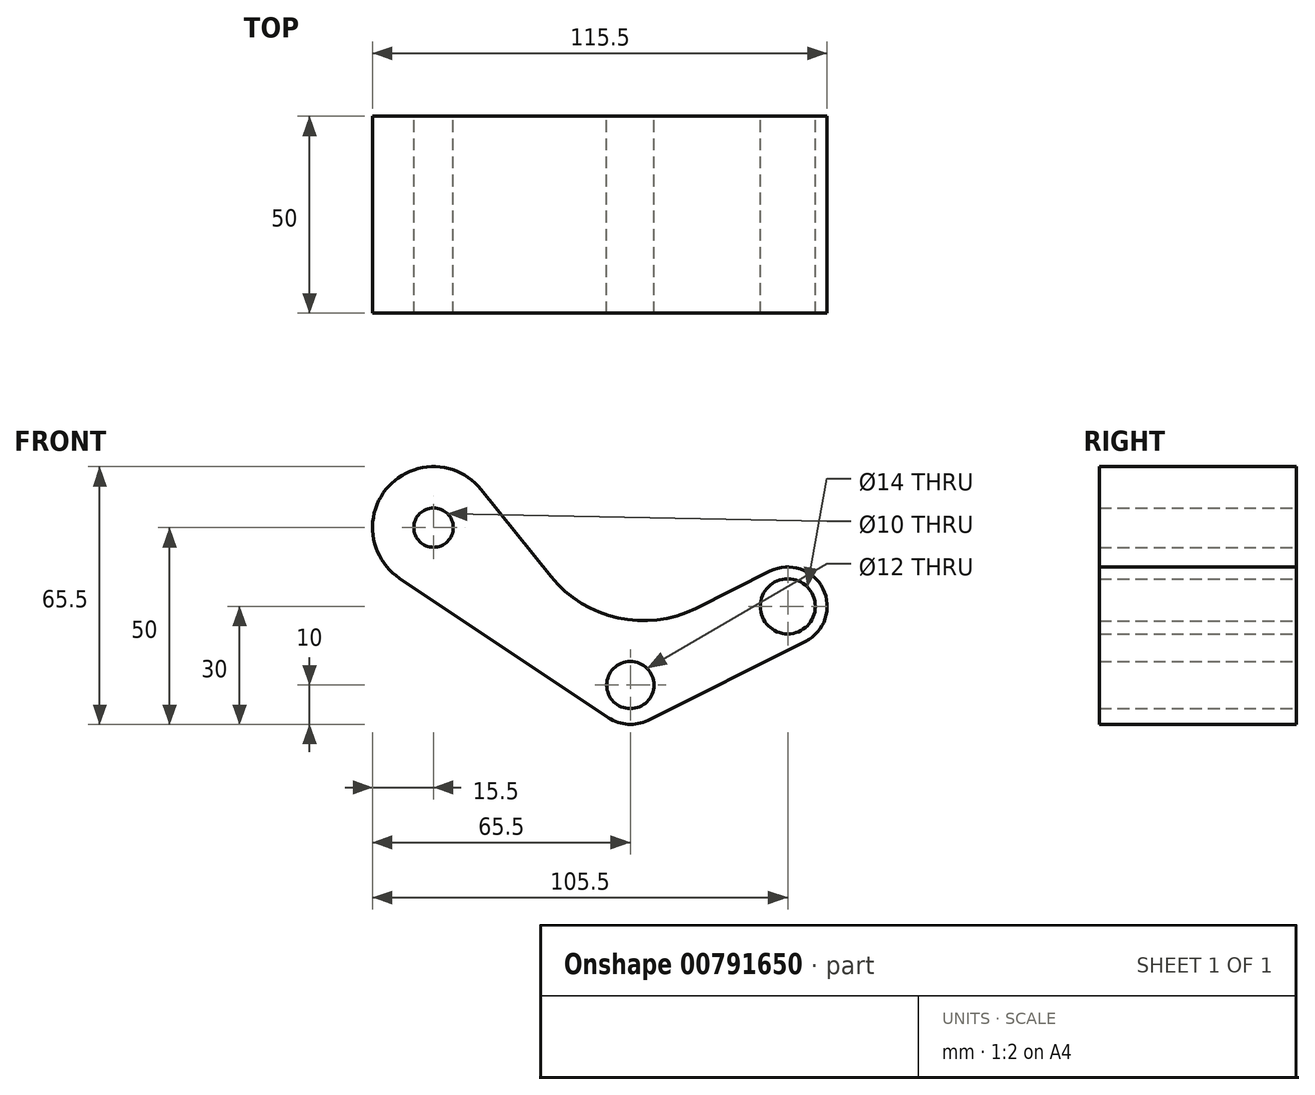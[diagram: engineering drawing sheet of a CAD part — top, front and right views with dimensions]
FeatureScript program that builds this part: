
annotation { "Feature Type Name" : "Feature", "Feature Type Description" : "" }
export const myFeature = defineFeature(function(context is Context, id is Id, definition is map)
    precondition{}
    {
        {
            var Q0;
            Q0=qCreatedBy(makeId("Front.planeOp"),FACE);
            var sketch = newSketch(context, id + "F0", { "sketchPlane" : qUnion([Q0])});
            skCircle(sketch, "E0", {"center": v(0, 0) * mm, "radius": 10 * mm});
            skCircle(sketch, "E1", {"center": v(0, 0) * mm, "radius": 6 * mm});
            skCircle(sketch, "E2", {"center": v(40, 20) * mm, "radius": 7 * mm});
            skCircle(sketch, "E3", {"center": v(40, 20) * mm, "radius": 10 * mm});
            skCircle(sketch, "E4", {"center": v(-50, 40) * mm, "radius": 15.5 * mm});
            skCircle(sketch, "E5", {"center": v(-50, 40) * mm, "radius": 5 * mm});
            skLineSegment(sketch, "E6", {"start": v(-58.6, 27.1) * mm, "end": v(-5.55, -8.32) * mm});
            skLineSegment(sketch, "E7", {"start": v(4.47, -8.94) * mm, "end": v(44.47, 11.06) * mm});
            skLineSegment(sketch, "E8", {"start": v(-37.91, 49.7) * mm, "end": v(-20.15, 27.57) * mm});
            skLineSegment(sketch, "E9", {"start": v(16.66, 19.51) * mm, "end": v(35.53, 28.94) * mm});
            skPoint(sketch, "E10.visualSharp", {"position": v(-5, 8.68) * mm});
            skArc(sketch, "E10.filletArc", {"start": v(-20.15, 27.57) * mm, "mid": v(-3.16, 17.04) * mm, "end": v(16.66, 19.51) * mm});
            skSolve(sketch);
        }
        {
            var Q0;
            {var subQ0=sQuery(id+"F0.wireOp",EDGE,"E6");Q0=makeQuery(id+"F0.imprint","IMPRINT",FACE,{"disambiguationData":[TD([[makeQuery(id+"F0.imprint","IMPRINT",EDGE,{"derivedFrom":subQ0}),1.0]])]});}
            var Q1;
            Q1=makeQuery(id+"F0.imprint","IMPRINT",FACE,{"disambiguationData":[TD([[makeQuery(id+"F0.imprint","IMPRINT",EDGE,{"derivedFrom":sQuery(id+"F0.wireOp",EDGE,"E5")}),-1.0]])]});
            var Q2;
            Q2=makeQuery(id+"F0.imprint","IMPRINT",FACE,{"disambiguationData":[TD([[makeQuery(id+"F0.imprint","IMPRINT",EDGE,{"derivedFrom":sQuery(id+"F0.wireOp",EDGE,"E1")}),-1.0]])]});
            var Q3;
            Q3=makeQuery(id+"F0.imprint","IMPRINT",FACE,{"disambiguationData":[TD([[makeQuery(id+"F0.imprint","IMPRINT",EDGE,{"derivedFrom":sQuery(id+"F0.wireOp",EDGE,"E2")}),-1.0]])]});
            extrude(context, id + "F1", {"entities" : qUnion([Q0, Q1, Q2, Q3]), "endBound" : BoundingType.SYMMETRIC, "depth" : 50 * mm, "offsetDistance" : 25.4 * mm});
        }
    });
